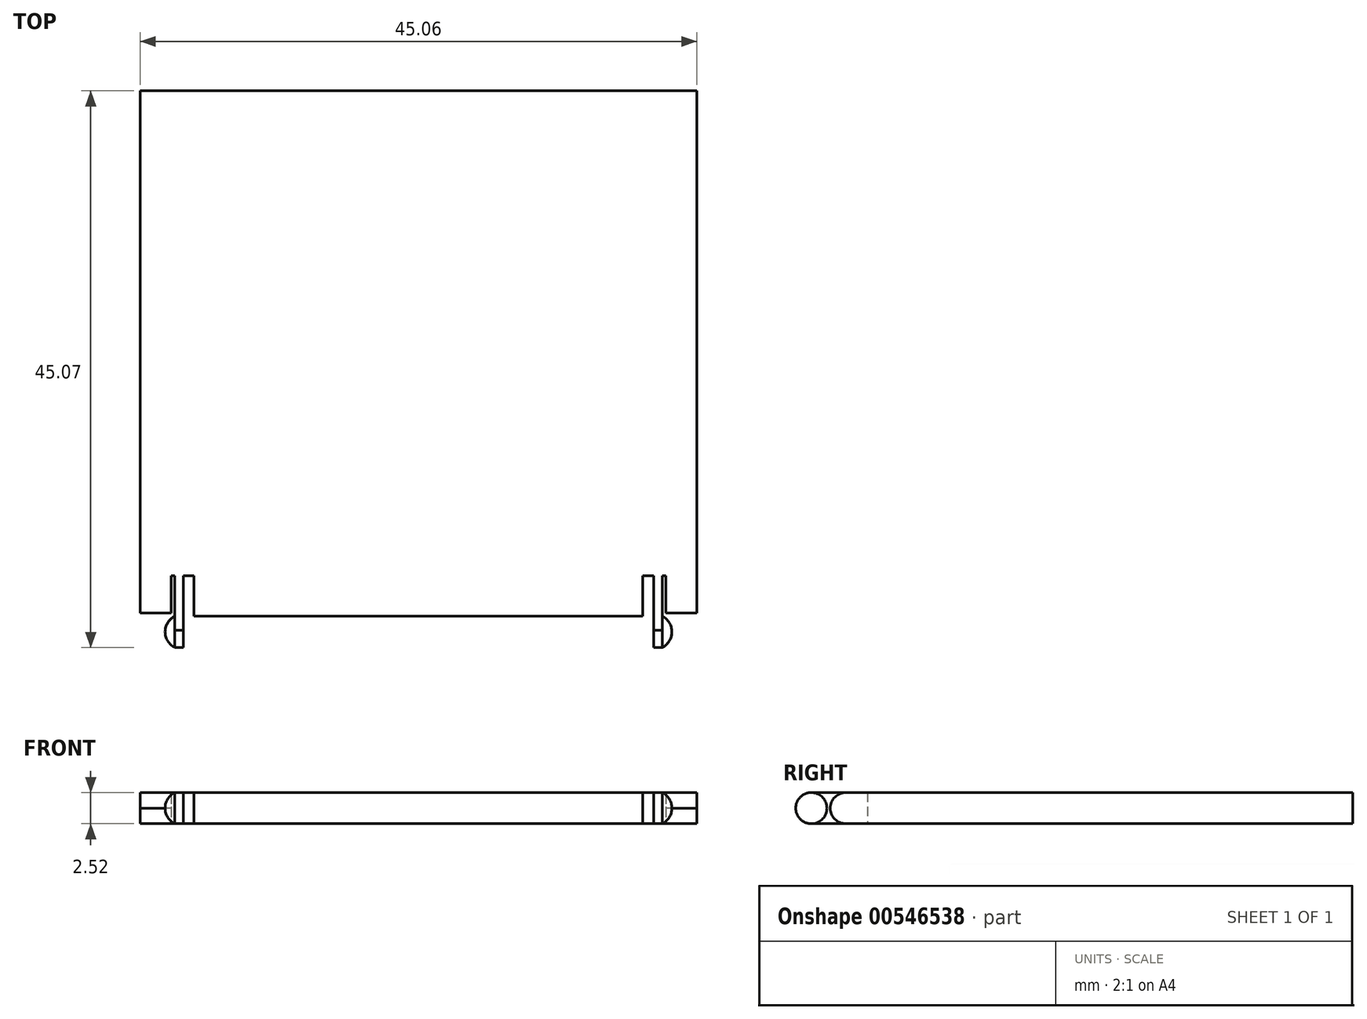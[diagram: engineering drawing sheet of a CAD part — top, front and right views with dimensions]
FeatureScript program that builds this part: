
annotation { "Feature Type Name" : "Feature", "Feature Type Description" : "" }
export const myFeature = defineFeature(function(context is Context, id is Id, definition is map)
    precondition{}
    {
        {
            var Q0;
            Q0=qCreatedBy(makeId("Top.planeOp"),FACE);
            var sketch = newSketch(context, id + "F0", { "sketchPlane" : qUnion([Q0])});
            skLineSegment(sketch, "E0.bottom", {"start": v(-20, -3.28) * mm, "end": v(-22.53, -3.28) * mm});
            skLineSegment(sketch, "E0.top", {"start": v(-20, -5.8) * mm, "end": v(-22.53, -5.8) * mm});
            skLineSegment(sketch, "E0.right", {"start": v(-22.53, -3.28) * mm, "end": v(-22.53, -5.8) * mm});
            skArc(sketch, "E1", {"start": v(-20, -3.28) * mm, "mid": v(-20.78, -4.55) * mm, "end": v(-20, -5.8) * mm});
            skLineSegment(sketch, "E2", {"start": v(-19.73, -3.28) * mm, "end": v(-19.04, -3.28) * mm});
            skLineSegment(sketch, "E3", {"start": v(-19.04, -3.28) * mm, "end": v(-19.04, -5.8) * mm});
            skLineSegment(sketch, "E4", {"start": v(-19.73, -3.28) * mm, "end": v(-19.73, -5.8) * mm});
            skLineSegment(sketch, "E5", {"start": v(-19.73, -5.8) * mm, "end": v(-19.04, -5.8) * mm});
            skArc(sketch, "E6", {"start": v(-19.73, -3.28) * mm, "mid": v(-20.5, -4.55) * mm, "end": v(-19.73, -5.8) * mm});
            skLineSegment(sketch, "E7", {"start": v(-19.73, -3.28) * mm, "end": v(-19.73, 0) * mm});
            skLineSegment(sketch, "E8", {"start": v(-19.73, 0) * mm, "end": v(-20, 0) * mm});
            skLineSegment(sketch, "E9", {"start": v(-20, 0) * mm, "end": v(-20, -3.01) * mm});
            skLineSegment(sketch, "E10", {"start": v(-20, -3.01) * mm, "end": v(-22.53, -3.01) * mm});
            skLineSegment(sketch, "E11", {"start": v(-22.53, -3.01) * mm, "end": v(-22.53, 39.26) * mm});
            skLineSegment(sketch, "E12", {"start": v(-22.53, 39.26) * mm, "end": v(0, 39.26) * mm});
            skLineSegment(sketch, "E13", {"start": v(0, -5.8) * mm, "end": v(-18.16, -5.8) * mm});
            skLineSegment(sketch, "E14", {"start": v(-18.16, -5.8) * mm, "end": v(-18.16, 0) * mm});
            skLineSegment(sketch, "E15", {"start": v(-19.04, -3.28) * mm, "end": v(-19.04, 0) * mm});
            skLineSegment(sketch, "E16", {"start": v(-19.04, 0) * mm, "end": v(-18.16, 0) * mm});
            skLineSegment(sketch, "E17.MirrorCS", {"start": v(19.73, -5.8) * mm, "end": v(19.04, -5.8) * mm});
            skLineSegment(sketch, "E18.MirrorCS", {"start": v(19.73, -3.28) * mm, "end": v(19.73, -5.8) * mm});
            skLineSegment(sketch, "E19.MirrorCS", {"start": v(19.73, -3.28) * mm, "end": v(19.04, -3.28) * mm});
            skLineSegment(sketch, "E20.MirrorCS", {"start": v(19.04, -3.28) * mm, "end": v(19.04, -5.8) * mm});
            skArc(sketch, "E21.MirrorCS", {"start": v(19.73, -3.28) * mm, "mid": v(20.5, -4.55) * mm, "end": v(19.73, -5.8) * mm});
            skLineSegment(sketch, "E22.MirrorCS", {"start": v(20, -3.28) * mm, "end": v(22.53, -3.28) * mm});
            skArc(sketch, "E23.MirrorCS", {"start": v(20, -3.28) * mm, "mid": v(20.78, -4.55) * mm, "end": v(20, -5.8) * mm});
            skLineSegment(sketch, "E24.MirrorCS", {"start": v(20, -3.01) * mm, "end": v(22.53, -3.01) * mm});
            skLineSegment(sketch, "E25.MirrorCS", {"start": v(19.73, 0) * mm, "end": v(20, 0) * mm});
            skLineSegment(sketch, "E26.MirrorCS", {"start": v(19.73, -3.28) * mm, "end": v(19.73, 0) * mm});
            skLineSegment(sketch, "E27.MirrorCS", {"start": v(19.04, -3.28) * mm, "end": v(19.04, 0) * mm});
            skLineSegment(sketch, "E28.MirrorCS", {"start": v(20, 0) * mm, "end": v(20, -3.01) * mm});
            skLineSegment(sketch, "E29.MirrorCS", {"start": v(19.04, 0) * mm, "end": v(18.16, 0) * mm});
            skLineSegment(sketch, "E30.MirrorCS", {"start": v(18.16, -5.8) * mm, "end": v(18.16, 0) * mm});
            skLineSegment(sketch, "E31.MirrorCS", {"start": v(22.53, -3.28) * mm, "end": v(22.53, -5.8) * mm});
            skLineSegment(sketch, "E32.MirrorCS", {"start": v(20, -5.8) * mm, "end": v(22.53, -5.8) * mm});
            skLineSegment(sketch, "E33.MirrorCS", {"start": v(0, -5.8) * mm, "end": v(18.16, -5.8) * mm});
            skLineSegment(sketch, "E34.MirrorCS", {"start": v(22.53, 39.26) * mm, "end": v(0, 39.26) * mm});
            skLineSegment(sketch, "E35.MirrorCS", {"start": v(22.53, -3.01) * mm, "end": v(22.53, 39.26) * mm});
            skLineSegment(sketch, "E36", {"start": v(19.73, 0) * mm, "end": v(19.04, 0) * mm});
            skLineSegment(sketch, "E37", {"start": v(-19.04, 0) * mm, "end": v(-19.73, 0) * mm});
            skLineSegment(sketch, "E38", {"start": v(-19.73, -4.55) * mm, "end": v(-20.5, -4.55) * mm});
            skLineSegment(sketch, "E39", {"start": v(-19.73, -4.55) * mm, "end": v(-19.04, -4.55) * mm});
            skLineSegment(sketch, "E40", {"start": v(20.5, -4.55) * mm, "end": v(19.04, -4.55) * mm});
            skSolve(sketch);
        }
        {
            var Q0;
            {var subQ3=sQuery(id+"F0.wireOp",EDGE,"E38");Q0=makeQuery(id+"F0.imprint","IMPRINT",FACE,{"disambiguationData":[TD([[makeQuery(id+"F0.imprint","IMPRINT",EDGE,{"derivedFrom":subQ3}),1.0]])]});}
            var Q1;
            {var subQ0=sQuery(id+"F0.wireOp",EDGE,"E21.MirrorCS");var subQ3=sQuery(id+"F0.wireOp",EDGE,"E40");var subQ5=makeQuery(id+"F0.imprint","INTERSECT",VERTEX,{"derivedFrom":[subQ0,subQ3]});Q1=makeQuery(id+"F0.imprint","IMPRINT",FACE,{"disambiguationData":[TD([[makeQuery(id+"F0.imprint","IMPRINT",EDGE,{"disambiguationData":[TD([[subQ5,-1.0]])],"derivedFrom":subQ3}),1.0]])]});}
            var Q2;
            {var subQ0=sQuery(id+"F0.wireOp",EDGE,"E17.MirrorCS");Q2=makeQuery(id+"F0.imprint","IMPRINT",FACE,{"disambiguationData":[TD([[makeQuery(id+"F0.imprint","IMPRINT",EDGE,{"derivedFrom":subQ0}),-1.0]])]});}
            var Q3;
            {var subQ0=sQuery(id+"F0.wireOp",EDGE,"E5");Q3=makeQuery(id+"F0.imprint","IMPRINT",FACE,{"disambiguationData":[TD([[makeQuery(id+"F0.imprint","IMPRINT",EDGE,{"derivedFrom":subQ0}),1.0]])]});}
            var Q4;
            Q4=sQuery(id+"F0.wireOp",EDGE,"E39");
            revolve(context, id + "F1", {"entities" : qUnion([Q0, Q1, Q2, Q3]), "axis" : qUnion([Q4]), "revolveType" : RevolveType.FULL});
        }
        {
            var Q0;
            Q0=makeQuery(id+"F0.imprint","IMPRINT",FACE,{"disambiguationData":[TD([[makeQuery(id+"F0.imprint","IMPRINT",EDGE,{"derivedFrom":sQuery(id+"F0.wireOp",EDGE,"E8")}),-1.0]])]});
            var Q1;
            Q1=makeQuery(id+"F0.imprint","IMPRINT",FACE,{"disambiguationData":[TD([[makeQuery(id+"F0.imprint","IMPRINT",EDGE,{"derivedFrom":sQuery(id+"F0.wireOp",EDGE,"E2")}),1.0]])]});
            var Q2;
            Q2=makeQuery(id+"F0.imprint","IMPRINT",FACE,{"disambiguationData":[TD([[makeQuery(id+"F0.imprint","IMPRINT",EDGE,{"derivedFrom":sQuery(id+"F0.wireOp",EDGE,"E19.MirrorCS")}),-1.0]])]});
            var Q3;
            Q3 = qSketchRegion(id + "FatAwkocNUZdNjW_1", true);
            var Q4;
            {var subQ0=sQuery(id+"F0.wireOp",EDGE,"E2");Q4=makeQuery(id+"F0.imprint","IMPRINT",FACE,{"disambiguationData":[TD([[makeQuery(id+"F0.imprint","IMPRINT",EDGE,{"derivedFrom":subQ0}),-1.0]])]});}
            var Q5;
            {var subQ0=sQuery(id+"F0.wireOp",EDGE,"E19.MirrorCS");Q5=makeQuery(id+"F0.imprint","IMPRINT",FACE,{"disambiguationData":[TD([[makeQuery(id+"F0.imprint","IMPRINT",EDGE,{"derivedFrom":subQ0}),1.0]])]});}
            extrude(context, id + "F2", {"entities" : qUnion([Q0, Q1, Q2, Q3, Q4, Q5]), "operationType" : NewBodyOperationType.ADD, "endBound" : BoundingType.SYMMETRIC, "depth" : 2.5 * mm, "offsetDistance" : 25.4 * mm});
        }
        {
            var Q0;
            Q0=makeQuery(id+"F2.opExtrude","SWEPT_FACE",FACE,{"disambiguationData":[OSD([sQuery(id+"F0.wireOp",EDGE,"E13"),sQuery(id+"F0.wireOp",EDGE,"E33.MirrorCS")])]});
            extrude(context, id + "F3", {"entities" : qUnion([Q0]), "operationType" : NewBodyOperationType.REMOVE, "oppositeDirection" : true, "depth" : 2.54 * mm, "offsetDistance" : 25.4 * mm});
        }
        {
            var Q0;
            {var subQ0=sQuery(id+"F0.wireOp",EDGE,"E33.MirrorCS");var subQ1=sQuery(id+"F0.wireOp",EDGE,"E13");Q0=makeQuery(id+"F3.boolean.opBoolean","COPY",EDGE,{"derivedFrom":makeQuery(id+"F3.opExtrude","CAP_EDGE",EDGE,{"disambiguationData":[OSD([subQ1,subQ0]),TDD([makeQuery(id+"F2.opExtrude","CAP_EDGE",EDGE,{"disambiguationData":[OSD([subQ1,subQ0])],"isStart":false})])],"isStart":false})});}
            var Q1;
            {var subQ0=sQuery(id+"F0.wireOp",EDGE,"E33.MirrorCS");var subQ1=sQuery(id+"F0.wireOp",EDGE,"E13");Q1=makeQuery(id+"F3.boolean.opBoolean","COPY",EDGE,{"derivedFrom":makeQuery(id+"F3.opExtrude","CAP_EDGE",EDGE,{"disambiguationData":[OSD([subQ1,subQ0]),TDD([makeQuery(id+"F2.opExtrude","CAP_EDGE",EDGE,{"disambiguationData":[OSD([subQ1,subQ0])],"isStart":true})])],"isStart":false})});}
            var Q2;
            Q2=makeQuery(id+"F2.opExtrude","CAP_EDGE",EDGE,{"disambiguationData":[OSD([sQuery(id+"F0.wireOp",EDGE,"E10")])],"isStart":false});
            var Q3;
            Q3=makeQuery(id+"F2.opExtrude","CAP_EDGE",EDGE,{"disambiguationData":[OSD([sQuery(id+"F0.wireOp",EDGE,"E10")])],"isStart":true});
            var Q4;
            Q4=makeQuery(id+"F2.opExtrude","CAP_EDGE",EDGE,{"disambiguationData":[OSD([sQuery(id+"F0.wireOp",EDGE,"E24.MirrorCS")])],"isStart":false});
            var Q5;
            Q5=makeQuery(id+"F2.opExtrude","CAP_EDGE",EDGE,{"disambiguationData":[OSD([sQuery(id+"F0.wireOp",EDGE,"E24.MirrorCS")])],"isStart":true});
            fillet(context, id + "F4", {"entities" : qUnion([Q0, Q1, Q2, Q3, Q4, Q5]), "radius" : 1.27 * mm, "tangentPropagation" : true, "allowEdgeOverflow" : false});
        }
    });
